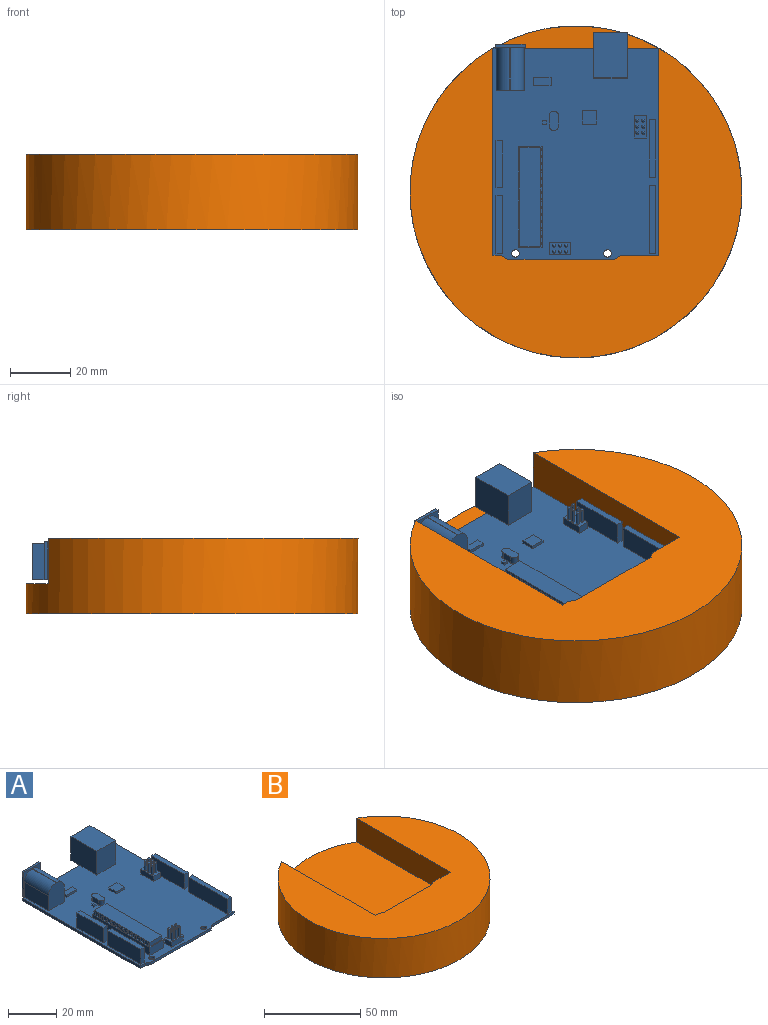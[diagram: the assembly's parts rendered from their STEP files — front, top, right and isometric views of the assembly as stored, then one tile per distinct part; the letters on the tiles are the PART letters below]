
ASSEMBLY  parts=2 mates=1
PART A: 244 faces, bbox 55x75.2x13.8 mm
  f0: plane 7x4mm, normal (0,0,1), area 23.3mm2, adj f194,f195,f196,f197,f226,f227,f228,f229
  f1: plane 7.5x4mm, normal (0,0,1), area 25.3mm2, adj f190,f191,f192,f193,f220,f221,f222,f223
  f2: plane 70x55mm, normal (0,0,1), area 3025.5mm2, adj f49,f50,f51,f52,f54,f55,f56,f57
  f3: plane 8.98x8.63mm, normal (0,1,0), area 52mm2, adj f179,f180,f181,f182,f183,f184,f185,f186
  f4: plane 1.5x0.4mm, normal (0,1,0), area 0.6mm2, adj f6,f46,f48,f178
  f5: plane 1.5x0.4mm, normal (0,-1,0), area 0.6mm2, adj f6,f46,f48,f178
  f6: plane 0.75x0.4mm, normal (0,0,1), area 0.3mm2, adj f4,f5,f46,f178
  f7: plane 1.5x0.4mm, normal (0,1,0), area 0.6mm2, adj f9,f46,f48,f177
  f8: plane 1.5x0.4mm, normal (0,-1,0), area 0.6mm2, adj f9,f46,f48,f177
  f9: plane 0.75x0.4mm, normal (0,0,1), area 0.3mm2, adj f7,f8,f46,f177
  f10: plane 1.5x0.4mm, normal (0,1,0), area 0.6mm2, adj f12,f46,f48,f176
  f11: plane 1.5x0.4mm, normal (0,-1,0), area 0.6mm2, adj f12,f46,f48,f176
  f12: plane 0.75x0.4mm, normal (0,0,1), area 0.3mm2, adj f10,f11,f46,f176
  f13: plane 1.5x0.4mm, normal (0,1,0), area 0.6mm2, adj f15,f46,f48,f175
  f14: plane 1.5x0.4mm, normal (0,-1,0), area 0.6mm2, adj f15,f46,f48,f175
  f15: plane 0.75x0.4mm, normal (0,0,1), area 0.3mm2, adj f13,f14,f46,f175
  f16: plane 1.5x0.4mm, normal (0,1,0), area 0.6mm2, adj f18,f46,f48,f174
  f17: plane 1.5x0.4mm, normal (0,-1,0), area 0.6mm2, adj f18,f46,f48,f174
  f18: plane 0.75x0.4mm, normal (0,0,1), area 0.3mm2, adj f16,f17,f46,f174
  f19: plane 1.5x0.4mm, normal (0,1,0), area 0.6mm2, adj f21,f46,f48,f173
  f20: plane 1.5x0.4mm, normal (0,-1,0), area 0.6mm2, adj f21,f46,f48,f173
  f21: plane 0.75x0.4mm, normal (0,0,1), area 0.3mm2, adj f19,f20,f46,f173
  f22: plane 1.5x0.4mm, normal (0,1,0), area 0.6mm2, adj f24,f46,f48,f172
  f23: plane 1.5x0.4mm, normal (0,-1,0), area 0.6mm2, adj f24,f46,f48,f172
  f24: plane 0.75x0.4mm, normal (0,0,1), area 0.3mm2, adj f22,f23,f46,f172
  f25: plane 1.5x0.4mm, normal (0,1,0), area 0.6mm2, adj f27,f46,f48,f171
  f26: plane 1.5x0.4mm, normal (0,-1,0), area 0.6mm2, adj f27,f46,f48,f171
  f27: plane 0.75x0.4mm, normal (0,0,1), area 0.3mm2, adj f25,f26,f46,f171
  f28: plane 1.5x0.4mm, normal (0,1,0), area 0.6mm2, adj f30,f46,f48,f170
  f29: plane 1.5x0.4mm, normal (0,-1,0), area 0.6mm2, adj f30,f46,f48,f170
  f30: plane 0.75x0.4mm, normal (0,0,1), area 0.3mm2, adj f28,f29,f46,f170
  f31: plane 1.5x0.4mm, normal (0,1,0), area 0.6mm2, adj f33,f46,f48,f169
  f32: plane 1.5x0.4mm, normal (0,-1,0), area 0.6mm2, adj f33,f46,f48,f169
  f33: plane 0.75x0.4mm, normal (0,0,1), area 0.3mm2, adj f31,f32,f46,f169
  f34: plane 1.5x0.4mm, normal (0,1,0), area 0.6mm2, adj f36,f46,f48,f168
  f35: plane 1.5x0.4mm, normal (0,-1,0), area 0.6mm2, adj f36,f46,f48,f168
  f36: plane 0.75x0.4mm, normal (0,0,1), area 0.3mm2, adj f34,f35,f46,f168
  f37: plane 1.5x0.4mm, normal (0,1,0), area 0.6mm2, adj f39,f46,f48,f167
  f38: plane 1.5x0.4mm, normal (0,-1,0), area 0.6mm2, adj f39,f46,f48,f167
  f39: plane 0.75x0.4mm, normal (0,0,1), area 0.3mm2, adj f37,f38,f46,f167
  f40: plane 1.5x0.4mm, normal (0,1,0), area 0.6mm2, adj f42,f46,f48,f166
  f41: plane 1.5x0.4mm, normal (0,-1,0), area 0.6mm2, adj f42,f46,f48,f166
  f42: plane 0.75x0.4mm, normal (0,0,1), area 0.3mm2, adj f40,f41,f46,f166
  f43: plane 1.5x0.4mm, normal (0,1,0), area 0.6mm2, adj f45,f46,f48,f165
  f44: plane 1.5x0.4mm, normal (0,-1,0), area 0.6mm2, adj f45,f46,f48,f165
  f45: plane 0.75x0.4mm, normal (0,0,1), area 0.3mm2, adj f43,f44,f46,f165
  f46: plane 32.63x2mm, normal (1,0,0), area 49.5mm2, adj f4,f5,f6,f7,f8,f9,f10,f11
  f47: plane 32.63x2mm, normal (-1,0,0), area 49.5mm2, adj f48,f106,f107,f108,f109,f110,f111,f112
  f48: plane 33.63x7.95mm, normal (0,0,1), area 32.2mm2, adj f4,f5,f7,f8,f10,f11,f13,f14
  f49: plane 33.63x4mm, normal (-1,0,0), area 134.5mm2, adj f2,f48,f50,f52
  f50: plane 7.95x4mm, normal (0,-1,0), area 31.8mm2, adj f2,f48,f49,f51
  f51: plane 33.63x4mm, normal (1,0,0), area 134.5mm2, adj f2,f48,f50,f52
  f52: plane 7.95x4mm, normal (0,1,0), area 31.8mm2, adj f2,f48,f49,f51
  f53: plane 6.98x6.98mm, normal (0,1,0), area 37.5mm2, adj f103,f104
  f54: plane 68.67x1.25mm, normal (1,0,0), area 85.8mm2, adj f2,f55,f58,f95
  f55: plane 55x1.25mm, normal (0,1,0), area 68.8mm2, adj f2,f54,f56,f58,f79,f84
  f56: plane 68.67x1.25mm, normal (-1,0,0), area 85.8mm2, adj f2,f55,f58,f92
  f57: plane 35.3x1.25mm, normal (0,-1,0), area 44.1mm2, adj f2,f58,f93,f94
  f58: plane 70x55mm, normal (0,0,-1), area 3816.6mm2, adj f54,f55,f56,f57,f92,f93,f94,f95
  f59: plane 7.5x2.22mm, normal (0,-1,0), area 16.7mm2, adj f2,f60,f62,f63
  f60: plane 22.58x7.5mm, normal (1,0,0), area 169.3mm2, adj f2,f59,f61,f63
  f61: plane 7.5x2.22mm, normal (0,1,0), area 16.7mm2, adj f2,f60,f62,f63
  f62: plane 22.58x7.5mm, normal (-1,0,0), area 169.3mm2, adj f2,f59,f61,f63
  f63: plane 22.58x2.22mm, normal (0,0,1), area 50.1mm2, adj f59,f60,f61,f62
  f64: plane 19.27x7.5mm, normal (-1,0,0), area 144.5mm2, adj f2,f65,f67,f68
  f65: plane 7.5x2.22mm, normal (0,-1,0), area 16.7mm2, adj f2,f64,f66,f68
  f66: plane 19.27x7.5mm, normal (1,0,0), area 144.5mm2, adj f2,f65,f67,f68
  f67: plane 7.5x2.22mm, normal (0,1,0), area 16.7mm2, adj f2,f64,f66,f68
  f68: plane 19.27x2.22mm, normal (0,0,1), area 42.8mm2, adj f64,f65,f66,f67
  f69: plane 19.1x7.5mm, normal (-1,0,0), area 143.2mm2, adj f2,f70,f72,f73
  f70: plane 7.5x2.22mm, normal (0,-1,0), area 16.7mm2, adj f2,f69,f71,f73
  f71: plane 19.1x7.5mm, normal (1,0,0), area 143.2mm2, adj f2,f70,f72,f73
  f72: plane 7.5x2.22mm, normal (0,1,0), area 16.7mm2, adj f2,f69,f71,f73
  f73: plane 19.1x2.22mm, normal (0,0,1), area 42.4mm2, adj f69,f70,f71,f72
  f74: plane 15.53x7.5mm, normal (1,0,0), area 116.5mm2, adj f2,f75,f77,f78
  f75: plane 7.5x2.22mm, normal (0,1,0), area 16.7mm2, adj f2,f74,f76,f78
  f76: plane 15.53x7.5mm, normal (-1,0,0), area 116.5mm2, adj f2,f75,f77,f78
  f77: plane 7.5x2.22mm, normal (0,-1,0), area 16.7mm2, adj f2,f74,f76,f78
  f78: plane 15.53x2.22mm, normal (0,0,1), area 34.5mm2, adj f74,f75,f76,f77
  f79: plane 9.89x1.2mm, normal (0,0,-1), area 11.7mm2, adj f55,f80,f82,f98,f99,f101,f102
  f80: plane 14.15x7.5mm, normal (-1,0,0), area 106.1mm2, adj f2,f79,f81,f90,f98
  f81: plane 12x9.24mm, normal (0,-1,0), area 102.2mm2, adj f2,f80,f82,f83,f90,f91
  f82: plane 14.15x7.5mm, normal (1,0,0), area 106.1mm2, adj f2,f79,f81,f91,f98
  f83: plane 14.15x0.24mm, normal (0,0,1), area 3.4mm2, adj f81,f90,f91,f98
  f84: plane 11.11x5.16mm, normal (0,0,-1), area 57.3mm2, adj f55,f85,f87,f88
  f85: plane 15.05x12mm, normal (-1,0,0), area 180.6mm2, adj f2,f84,f86,f88,f89
  f86: plane 12x11.11mm, normal (0,-1,0), area 133.3mm2, adj f2,f85,f87,f89
  f87: plane 15.05x12mm, normal (1,0,0), area 180.6mm2, adj f2,f84,f86,f88,f89
  f88: plane 12x11.11mm, normal (0,1,0), area 60.1mm2, adj f84,f85,f87,f89,f179,f180,f181,f182
  f89: plane 15.05x11.11mm, normal (0,0,1), area 167.2mm2, adj f85,f86,f87,f88
  f90: cylinder r=4.5mm len=14.15mm, axis (0,1,0), area 100mm2, adj f80,f81,f83,f98
  f91: cylinder r=4.5mm len=14.15mm, axis (0,-1,0), area 100mm2, adj f81,f82,f83,f98
  f92: plane 2.98x1.25mm, normal (0,-1,0), area 3.7mm2, adj f2,f56,f58,f93
  f93: plane 2.01x1.33mm, normal (-0.55,-0.83,0), area 3mm2, adj f2,f57,f58,f92
  f94: plane 2.01x1.33mm, normal (0.55,-0.83,0), area 3mm2, adj f2,f57,f58,f95
  f95: plane 12.71x1.25mm, normal (0,-1,0), area 15.9mm2, adj f2,f54,f58,f94
  f96: cylinder r=1.25mm len=2.5mm, axis (0,0,1), area 9.8mm2, adj f2,f58
  f97: cylinder r=1.25mm len=2.5mm, axis (0,0,1), area 9.8mm2, adj f2,f58
  f98: plane 12.57x9.89mm, normal (0,-1,0), area 22.1mm2, adj f79,f80,f82,f83,f90,f91,f99,f100
  f99: plane 12.57x1mm, normal (-1,0,0), area 12.6mm2, adj f79,f98,f100,f102
  f100: plane 9.89x1mm, normal (0,0,1), area 9.9mm2, adj f98,f99,f101,f102
  f101: plane 12.57x1mm, normal (1,0,0), area 12.6mm2, adj f79,f98,f100,f102
  f102: plane 12.57x9.89mm, normal (0,1,0), area 86mm2, adj f79,f99,f100,f101,f103
  f103: cylinder r=3.49mm len=12mm, axis (0,1,0), area 263.3mm2, adj f53,f102
  f104: cylinder r=0.5mm len=8mm, axis (0,-1,0), area 25.1mm2, adj f53,f105
  f105: plane 1x1mm, normal (0,1,0), area 0.8mm2, adj f104
  f106: plane 6.95x2mm, normal (0,1,0), area 13.9mm2, adj f46,f47,f48,f108
  f107: plane 6.95x2mm, normal (0,-1,0), area 13.9mm2, adj f46,f47,f48,f108
  f108: plane 32.63x6.95mm, normal (0,0,1), area 226.7mm2, adj f46,f47,f106,f107
  f109: plane 1.5x0.4mm, normal (0,1,0), area 0.6mm2, adj f47,f48,f111,f164
  f110: plane 1.5x0.4mm, normal (0,-1,0), area 0.6mm2, adj f47,f48,f111,f164
  f111: plane 0.75x0.4mm, normal (0,0,1), area 0.3mm2, adj f47,f109,f110,f164
  f112: plane 1.5x0.4mm, normal (0,1,0), area 0.6mm2, adj f47,f48,f114,f163
  f113: plane 1.5x0.4mm, normal (0,-1,0), area 0.6mm2, adj f47,f48,f114,f163
  f114: plane 0.75x0.4mm, normal (0,0,1), area 0.3mm2, adj f47,f112,f113,f163
  f115: plane 1.5x0.4mm, normal (0,1,0), area 0.6mm2, adj f47,f48,f117,f162
  f116: plane 1.5x0.4mm, normal (0,-1,0), area 0.6mm2, adj f47,f48,f117,f162
  f117: plane 0.75x0.4mm, normal (0,0,1), area 0.3mm2, adj f47,f115,f116,f162
  f118: plane 1.5x0.4mm, normal (0,1,0), area 0.6mm2, adj f47,f48,f120,f161
  f119: plane 1.5x0.4mm, normal (0,-1,0), area 0.6mm2, adj f47,f48,f120,f161
  f120: plane 0.75x0.4mm, normal (0,0,1), area 0.3mm2, adj f47,f118,f119,f161
  f121: plane 1.5x0.4mm, normal (0,1,0), area 0.6mm2, adj f47,f48,f123,f160
  f122: plane 1.5x0.4mm, normal (0,-1,0), area 0.6mm2, adj f47,f48,f123,f160
  f123: plane 0.75x0.4mm, normal (0,0,1), area 0.3mm2, adj f47,f121,f122,f160
  f124: plane 1.5x0.4mm, normal (0,1,0), area 0.6mm2, adj f47,f48,f126,f159
  f125: plane 1.5x0.4mm, normal (0,-1,0), area 0.6mm2, adj f47,f48,f126,f159
  f126: plane 0.75x0.4mm, normal (0,0,1), area 0.3mm2, adj f47,f124,f125,f159
  f127: plane 1.5x0.4mm, normal (0,1,0), area 0.6mm2, adj f47,f48,f129,f158
  f128: plane 1.5x0.4mm, normal (0,-1,0), area 0.6mm2, adj f47,f48,f129,f158
  f129: plane 0.75x0.4mm, normal (0,0,1), area 0.3mm2, adj f47,f127,f128,f158
  f130: plane 1.5x0.4mm, normal (0,1,0), area 0.6mm2, adj f47,f48,f132,f157
  f131: plane 1.5x0.4mm, normal (0,-1,0), area 0.6mm2, adj f47,f48,f132,f157
  f132: plane 0.75x0.4mm, normal (0,0,1), area 0.3mm2, adj f47,f130,f131,f157
  f133: plane 1.5x0.4mm, normal (0,1,0), area 0.6mm2, adj f47,f48,f135,f156
  f134: plane 1.5x0.4mm, normal (0,-1,0), area 0.6mm2, adj f47,f48,f135,f156
  f135: plane 0.75x0.4mm, normal (0,0,1), area 0.3mm2, adj f47,f133,f134,f156
  f136: plane 1.5x0.4mm, normal (0,1,0), area 0.6mm2, adj f47,f48,f138,f155
  f137: plane 1.5x0.4mm, normal (0,-1,0), area 0.6mm2, adj f47,f48,f138,f155
  f138: plane 0.75x0.4mm, normal (0,0,1), area 0.3mm2, adj f47,f136,f137,f155
  f139: plane 1.5x0.4mm, normal (0,1,0), area 0.6mm2, adj f47,f48,f141,f154
  f140: plane 1.5x0.4mm, normal (0,-1,0), area 0.6mm2, adj f47,f48,f141,f154
  f141: plane 0.75x0.4mm, normal (0,0,1), area 0.3mm2, adj f47,f139,f140,f154
  f142: plane 1.5x0.4mm, normal (0,1,0), area 0.6mm2, adj f47,f48,f144,f153
  f143: plane 1.5x0.4mm, normal (0,-1,0), area 0.6mm2, adj f47,f48,f144,f153
  f144: plane 0.75x0.4mm, normal (0,0,1), area 0.3mm2, adj f47,f142,f143,f153
  f145: plane 1.5x0.4mm, normal (0,1,0), area 0.6mm2, adj f47,f48,f147,f152
  f146: plane 1.5x0.4mm, normal (0,-1,0), area 0.6mm2, adj f47,f48,f147,f152
  f147: plane 0.75x0.4mm, normal (0,0,1), area 0.3mm2, adj f47,f145,f146,f152
  f148: plane 1.5x0.4mm, normal (0,1,0), area 0.6mm2, adj f47,f48,f150,f151
  f149: plane 1.5x0.4mm, normal (0,-1,0), area 0.6mm2, adj f47,f48,f150,f151
  f150: plane 0.75x0.4mm, normal (0,0,1), area 0.3mm2, adj f47,f148,f149,f151
  f151: plane 1.5x0.75mm, normal (-1,0,0), area 1.1mm2, adj f48,f148,f149,f150
  f152: plane 1.5x0.75mm, normal (-1,0,0), area 1.1mm2, adj f48,f145,f146,f147
  f153: plane 1.5x0.75mm, normal (-1,0,0), area 1.1mm2, adj f48,f142,f143,f144
  f154: plane 1.5x0.75mm, normal (-1,0,0), area 1.1mm2, adj f48,f139,f140,f141
  f155: plane 1.5x0.75mm, normal (-1,0,0), area 1.1mm2, adj f48,f136,f137,f138
  f156: plane 1.5x0.75mm, normal (-1,0,0), area 1.1mm2, adj f48,f133,f134,f135
  f157: plane 1.5x0.75mm, normal (-1,0,0), area 1.1mm2, adj f48,f130,f131,f132
  f158: plane 1.5x0.75mm, normal (-1,0,0), area 1.1mm2, adj f48,f127,f128,f129
  f159: plane 1.5x0.75mm, normal (-1,0,0), area 1.1mm2, adj f48,f124,f125,f126
  f160: plane 1.5x0.75mm, normal (-1,0,0), area 1.1mm2, adj f48,f121,f122,f123
  f161: plane 1.5x0.75mm, normal (-1,0,0), area 1.1mm2, adj f48,f118,f119,f120
  f162: plane 1.5x0.75mm, normal (-1,0,0), area 1.1mm2, adj f48,f115,f116,f117
  f163: plane 1.5x0.75mm, normal (-1,0,0), area 1.1mm2, adj f48,f112,f113,f114
  f164: plane 1.5x0.75mm, normal (-1,0,0), area 1.1mm2, adj f48,f109,f110,f111
  f165: plane 1.5x0.75mm, normal (1,0,0), area 1.1mm2, adj f43,f44,f45,f48
  f166: plane 1.5x0.75mm, normal (1,0,0), area 1.1mm2, adj f40,f41,f42,f48
  f167: plane 1.5x0.75mm, normal (1,0,0), area 1.1mm2, adj f37,f38,f39,f48
  f168: plane 1.5x0.75mm, normal (1,0,0), area 1.1mm2, adj f34,f35,f36,f48
  f169: plane 1.5x0.75mm, normal (1,0,0), area 1.1mm2, adj f31,f32,f33,f48
  f170: plane 1.5x0.75mm, normal (1,0,0), area 1.1mm2, adj f28,f29,f30,f48
  f171: plane 1.5x0.75mm, normal (1,0,0), area 1.1mm2, adj f25,f26,f27,f48
  f172: plane 1.5x0.75mm, normal (1,0,0), area 1.1mm2, adj f22,f23,f24,f48
  f173: plane 1.5x0.75mm, normal (1,0,0), area 1.1mm2, adj f19,f20,f21,f48
  f174: plane 1.5x0.75mm, normal (1,0,0), area 1.1mm2, adj f16,f17,f18,f48
  f175: plane 1.5x0.75mm, normal (1,0,0), area 1.1mm2, adj f13,f14,f15,f48
  f176: plane 1.5x0.75mm, normal (1,0,0), area 1.1mm2, adj f10,f11,f12,f48
  f177: plane 1.5x0.75mm, normal (1,0,0), area 1.1mm2, adj f7,f8,f9,f48
  f178: plane 1.5x0.75mm, normal (1,0,0), area 1.1mm2, adj f4,f5,f6,f48
  f179: plane 10x6.73mm, normal (1,0,0), area 67.3mm2, adj f3,f88,f180,f184
  f180: plane 10x8.63mm, normal (0,0,1), area 86.3mm2, adj f3,f88,f179,f181
  f181: plane 10x6.73mm, normal (-1,0,0), area 67.3mm2, adj f3,f88,f180,f182
  f182: plane 10x2.24mm, normal (-0.76,0,-0.65), area 29.4mm2, adj f3,f88,f181,f183
  f183: plane 10x4.83mm, normal (0,0,-1), area 48.3mm2, adj f3,f88,f182,f184
  f184: plane 10x2.24mm, normal (0.76,0,-0.65), area 29.4mm2, adj f3,f88,f179,f183
  f185: plane 8x3.45mm, normal (-1,0,0), area 27.6mm2, adj f3,f186,f188,f189
  f186: plane 8x6.13mm, normal (0,0,1), area 49mm2, adj f3,f185,f187,f189
  f187: plane 8x3.45mm, normal (1,0,0), area 27.6mm2, adj f3,f186,f188,f189
  f188: plane 8x6.13mm, normal (0,0,-1), area 49mm2, adj f3,f185,f187,f189
  f189: plane 6.13x3.45mm, normal (0,1,0), area 21.2mm2, adj f185,f186,f187,f188
  f190: plane 7.5x2.5mm, normal (-1,0,0), area 18.7mm2, adj f1,f2,f191,f193
  f191: plane 4x2.5mm, normal (0,-1,0), area 10mm2, adj f1,f2,f190,f192
  f192: plane 7.5x2.5mm, normal (1,0,0), area 18.7mm2, adj f1,f2,f191,f193
  f193: plane 4x2.5mm, normal (0,1,0), area 10mm2, adj f1,f2,f190,f192
  f194: plane 4x2.5mm, normal (-1,0,0), area 10mm2, adj f0,f2,f195,f197
  f195: plane 7x2.5mm, normal (0,-1,0), area 17.5mm2, adj f0,f2,f194,f196
  f196: plane 4x2.5mm, normal (1,0,0), area 10mm2, adj f0,f2,f195,f197
  f197: plane 7x2.5mm, normal (0,1,0), area 17.5mm2, adj f0,f2,f194,f196
  f198: plane 3.5x2.5mm, normal (-1,0,0), area 8.8mm2, adj f2,f200,f201,f203
  f199: plane 3.5x2.5mm, normal (1,0,0), area 8.8mm2, adj f2,f200,f202,f204
  f200: plane 6.5x3mm, normal (0,0,1), area 17.6mm2, adj f198,f199,f201,f202,f203,f204
  f201: cylinder r=1.5mm len=2.5mm, axis (0,0,-1), area 5.9mm2, adj f2,f198,f200,f202
  f202: cylinder r=1.5mm len=2.5mm, axis (0,0,-1), area 5.9mm2, adj f2,f199,f200,f201
  f203: cylinder r=1.5mm len=2.5mm, axis (0,0,-1), area 5.9mm2, adj f2,f198,f200,f204
  f204: cylinder r=1.5mm len=2.5mm, axis (0,0,-1), area 5.9mm2, adj f2,f199,f200,f203
  f205: plane 2.66x1mm, normal (-1,0,0), area 2.7mm2, adj f2,f206,f208,f209
  f206: plane 5.95x1mm, normal (0,-1,0), area 6mm2, adj f2,f205,f207,f209
  f207: plane 2.66x1mm, normal (1,0,0), area 2.7mm2, adj f2,f206,f208,f209
  f208: plane 5.95x1mm, normal (0,1,0), area 6mm2, adj f2,f205,f207,f209
  f209: plane 5.95x2.66mm, normal (0,0,1), area 15.9mm2, adj f205,f206,f207,f208
  f210: plane 1.1x1mm, normal (-1,0,0), area 1.1mm2, adj f2,f211,f213,f214
  f211: plane 1.57x1mm, normal (0,-1,0), area 1.6mm2, adj f2,f210,f212,f214
  f212: plane 1.1x1mm, normal (1,0,0), area 1.1mm2, adj f2,f211,f213,f214
  f213: plane 1.57x1mm, normal (0,1,0), area 1.6mm2, adj f2,f210,f212,f214
  f214: plane 1.57x1.1mm, normal (0,0,1), area 1.7mm2, adj f210,f211,f212,f213
  f215: plane 4.54x1mm, normal (-1,0,0), area 4.5mm2, adj f2,f216,f218,f219
  f216: plane 4.86x1mm, normal (0,-1,0), area 4.9mm2, adj f2,f215,f217,f219
  f217: plane 4.54x1mm, normal (1,0,0), area 4.5mm2, adj f2,f216,f218,f219
  f218: plane 4.86x1mm, normal (0,1,0), area 4.9mm2, adj f2,f215,f217,f219
  f219: plane 4.86x4.54mm, normal (0,0,1), area 22.1mm2, adj f215,f216,f217,f218
  f220: cylinder r=0.5mm len=4.5mm, axis (0,0,-1), area 14.1mm2, adj f1,f237
  f221: cylinder r=0.5mm len=4.5mm, axis (0,0,-1), area 14.1mm2, adj f1,f238
  f222: cylinder r=0.5mm len=4.5mm, axis (0,0,-1), area 14.1mm2, adj f1,f235
  f223: cylinder r=0.5mm len=4.5mm, axis (0,0,-1), area 14.1mm2, adj f1,f232
  f224: cylinder r=0.5mm len=4.5mm, axis (0,0,-1), area 14.1mm2, adj f1,f233
  f225: cylinder r=0.5mm len=4.5mm, axis (0,0,-1), area 14.1mm2, adj f1,f234
  f226: cylinder r=0.5mm len=4.5mm, axis (0,0,-1), area 14.1mm2, adj f0,f239
  f227: cylinder r=0.5mm len=4.5mm, axis (0,0,-1), area 14.1mm2, adj f0,f236
  f228: cylinder r=0.5mm len=4.5mm, axis (0,0,-1), area 14.1mm2, adj f0,f242
  f229: cylinder r=0.5mm len=4.5mm, axis (0,0,-1), area 14.1mm2, adj f0,f241
  f230: cylinder r=0.5mm len=4.5mm, axis (0,0,-1), area 14.1mm2, adj f0,f240
  f231: cylinder r=0.5mm len=4.5mm, axis (0,0,-1), area 14.1mm2, adj f0,f243
  f232: sphere r=0.5mm, area 1.6mm2, adj f223
  f233: sphere r=0.5mm, area 1.6mm2, adj f224
  f234: sphere r=0.5mm, area 1.6mm2, adj f225
  f235: sphere r=0.5mm, area 1.6mm2, adj f222
  f236: sphere r=0.5mm, area 1.6mm2, adj f227
  f237: sphere r=0.5mm, area 1.6mm2, adj f220
  f238: sphere r=0.5mm, area 1.6mm2, adj f221
  f239: sphere r=0.5mm, area 1.6mm2, adj f226
  f240: sphere r=0.5mm, area 1.6mm2, adj f230
  f241: sphere r=0.5mm, area 1.6mm2, adj f229
  f242: sphere r=0.5mm, area 1.6mm2, adj f228
  f243: sphere r=0.5mm, area 1.6mm2, adj f231
PART B: 13 faces, bbox 110x110x25 mm
  f0: plane 77.37x55mm, normal (0,0,1), area 4090.6mm2, adj f1,f3,f4,f5,f6,f7,f8,f9
  f1: cylinder r=55mm len=110mm, axis (0,0,-1), area 7775.4mm2, adj f0,f2,f3,f9,f10
  f2: plane 110x110mm, normal (0,0,-1), area 9493.5mm2, adj f1,f11,f12
  f3: plane 68.67x15mm, normal (-1,0,0), area 1030mm2, adj f0,f1,f4,f10
  f4: plane 15x12.71mm, normal (0,1,0), area 190.7mm2, adj f0,f3,f5,f10
  f5: plane 15x2.01mm, normal (-0.55,0.83,0), area 36.1mm2, adj f0,f4,f6,f10
  f6: plane 35.3x15mm, normal (0,1,0), area 529.6mm2, adj f0,f5,f7,f10
  f7: plane 15x2.01mm, normal (0.55,0.83,0), area 36.1mm2, adj f0,f6,f8,f10
  f8: plane 15x2.98mm, normal (0,1,0), area 44.6mm2, adj f0,f7,f9,f10
  f9: plane 68.67x15mm, normal (1,0,0), area 1030mm2, adj f0,f1,f8,f10
  f10: plane 110x102.63mm, normal (0,0,1), area 5402.9mm2, adj f1,f3,f4,f5,f6,f7,f8,f9
  f11: cylinder r=1.25mm len=10mm, axis (0,0,1), area 78.5mm2, adj f0,f2
  f12: cylinder r=1.25mm len=10mm, axis (0,0,1), area 78.5mm2, adj f0,f2
PLACE A t=(98.48,-100.9,27.49)mm
PLACE B t=(98.48,-113.53,17.49)mm
MATE parallel A.f58 <-> B.f1  axis (0,0,-1) through (98.43,-100.6,27.49)mm
